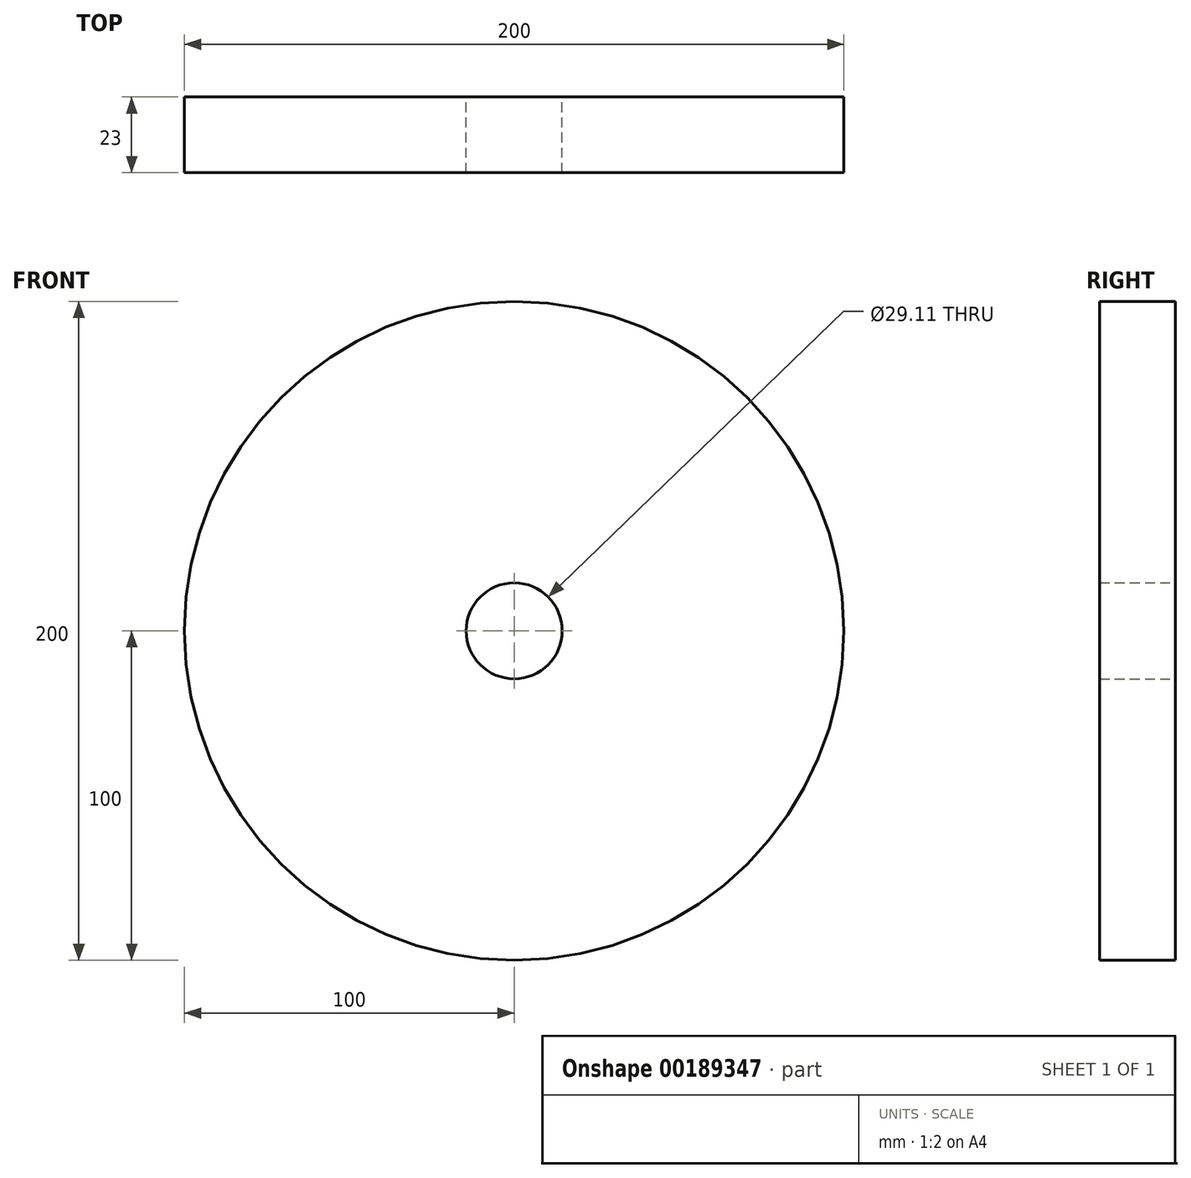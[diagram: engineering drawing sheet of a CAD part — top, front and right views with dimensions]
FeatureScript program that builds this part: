
annotation { "Feature Type Name" : "Feature", "Feature Type Description" : "" }
export const myFeature = defineFeature(function(context is Context, id is Id, definition is map)
    precondition{}
    {
        {
            var Q0;
            Q0=qCreatedBy(makeId("Front.planeOp"),FACE);
            var sketch = newSketch(context, id + "F0", { "sketchPlane" : qUnion([Q0])});
            skCircle(sketch, "E0", {"center": v(0, 0) * mm, "radius": 100 * mm});
            skCircle(sketch, "E1", {"center": v(0, 0) * mm, "radius": 55 * mm, "construction": true});
            skCircle(sketch, "E2", {"center": v(0, 0) * mm, "radius": 80 * mm, "construction": true});
            skCircle(sketch, "E3", {"center": v(0, 0) * mm, "radius": 14.56 * mm});
            skCircle(sketch, "E4", {"center": v(0, 0) * mm, "radius": 37.56 * mm});
            skSolve(sketch);
        }
        {
            var Q0;
            Q0=makeQuery(id+"F0.imprint","IMPRINT",FACE,{"disambiguationData":[TD([[makeQuery(id+"F0.imprint","IMPRINT",EDGE,{"derivedFrom":sQuery(id+"F0.wireOp",EDGE,"E0")}),1.0]])]});
            var Q1;
            Q1=makeQuery(id+"F0.imprint","IMPRINT",FACE,{"disambiguationData":[TD([[makeQuery(id+"F0.imprint","IMPRINT",EDGE,{"derivedFrom":sQuery(id+"F0.wireOp",EDGE,"E3")}),-1.0]])]});
            extrude(context, id + "F1", {"entities" : qUnion([Q0, Q1]), "depth" : 23 * mm});
        }
    });
